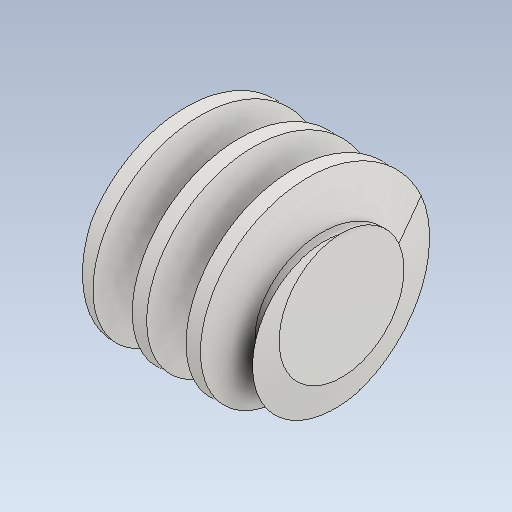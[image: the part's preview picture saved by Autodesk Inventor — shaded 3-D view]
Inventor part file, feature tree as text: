
AUTODESK INVENTOR PART (.ipt)
format: ipt  version: 2021 (Build 250183000, 183)  size: 291,328 bytes
history: native  units: mm (DEFAULTED — no unit token found)
features: other x6, chamfer x2, pattern_circular x2, extrude x1, sketch x1
ambient origin geometry x6: Origin, XZ Plane, X Axis, Y Axis, Z Axis, Center Point
bodies: Solid1 (feature_tree)
feature tree (12):
  extrude  "Base Body"  Depth=10.0mm
  chamfer  "Chamfer1"  Distance=40.0mm
  chamfer  "Chamfer2"  [1 undecoded]
  other  "Tooth Sketch"
  other  "Tooth"
  pattern_circular  "Tooth Pattern"  [2 undecoded]
  other  "Left Tooth"
  pattern_circular  "Left Tooth Pattern"  [2 undecoded]
  other  "Base Body Sketch"
  sketch  "Sketch5"  dims[d4=40.0mm d5=48.0mm d6=40.0mm d7=0.0mm d8=3.42132mm d9=9.4mm d10=3.42132mm d11=9.4mm d12=19.198622mm d14=3.1425mm d24=19.198622mm d25=31.415927mm d26=3.141593mm d27=14.6mm d28=20.0mm d29=24.24mm d30=12.566371mm d31=10.0mm d32=60.0mm d33=0.0mm d34=90.0deg d35=90.0deg d36=0.0mm d37=0.0mm d44=10.0mm d46=360.0deg d47=45.0deg d48=45.0deg d49=68.0168mm d50=0.0mm d54=0.0mm d56=0.0mm d59=40.0mm d60=10.0mm d61=0.0mm d62=12.566371mm d63=10.0mm d64=60.0mm d65=0.0mm d66=90.0deg d67=90.0deg d68=0.0mm d69=0.0mm d70=10.0mm d71=10.0mm d72=10.0mm d73=360.0deg d75=10.0mm d76=10.0mm d77=0.0mm d79=68.0168mm d80=0.0mm]
  other  "Srf1"
  other  "Pitch Diameter"
note: 5 required parameter values undecoded (feature->parameter linkage not recoverable at this tier; creation-order binding heuristic only, values carry confidence <= 0.55)
